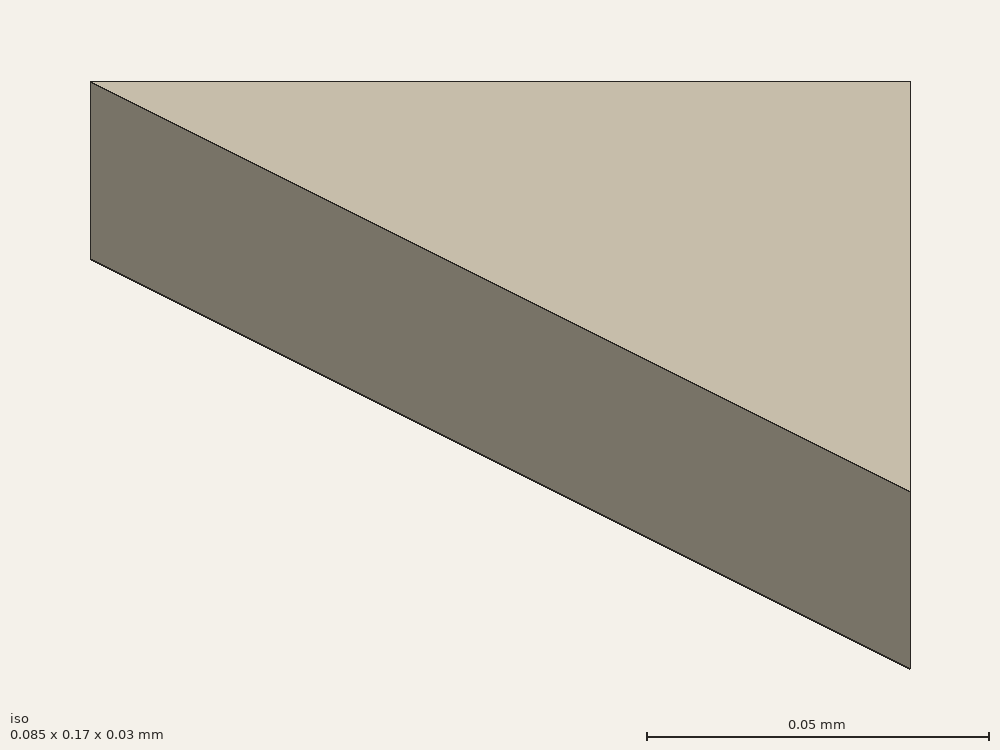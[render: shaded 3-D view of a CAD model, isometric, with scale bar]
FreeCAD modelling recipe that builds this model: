
FCSTD DOCUMENT  (FreeCAD 0.15R4671 (Git))
Label: triangle5
License: All rights reserved
LicenseURL: http://en.wikipedia.org/wiki/All_rights_reserved
objects: Sketcher::SketchObject×1, PartDesign::Pad×1
note: 3 computed .brp shape members not serialized (recipe doc carries the construction recipe); baked Part::Feature solids carry a one-line shape summary decoded from their .brp

FEATURE [Sketcher::SketchObject] Sketch
  sketch-geometry (3):
    g0: LineSegment StartX=0.0565685 StartY=0 StartZ=0 EndX=-0.0282843 EndY=0.0848528 EndZ=0
    g1: LineSegment StartX=-0.0282843 StartY=0.0848528 StartZ=0 EndX=-0.0282843 EndY=-0.0848528 EndZ=0
    g2: LineSegment StartX=-0.0282843 StartY=-0.0848528 StartZ=0 EndX=0.0565685 EndY=0 EndZ=0
  constraints (9):
    c: Coincident(g0,g1)
    c: Coincident(g1,g2)
    c: Coincident(g0,g2)
    c: Distance(g1,g0) = 0.12
    c: Perpendicular(g0,g2)
    c: Distance(g-1,g2) = 0.04
    c: Distance(g-1,g0) = 0.04
    c: Distance(g0) = 0.12
    c: Vertical(g1)
FEATURE [PartDesign::Pad] Pad
  Length = 0.03
  Length2 = 100
  Midplane = true
  Sketch = -> Sketch
  Type = 0
